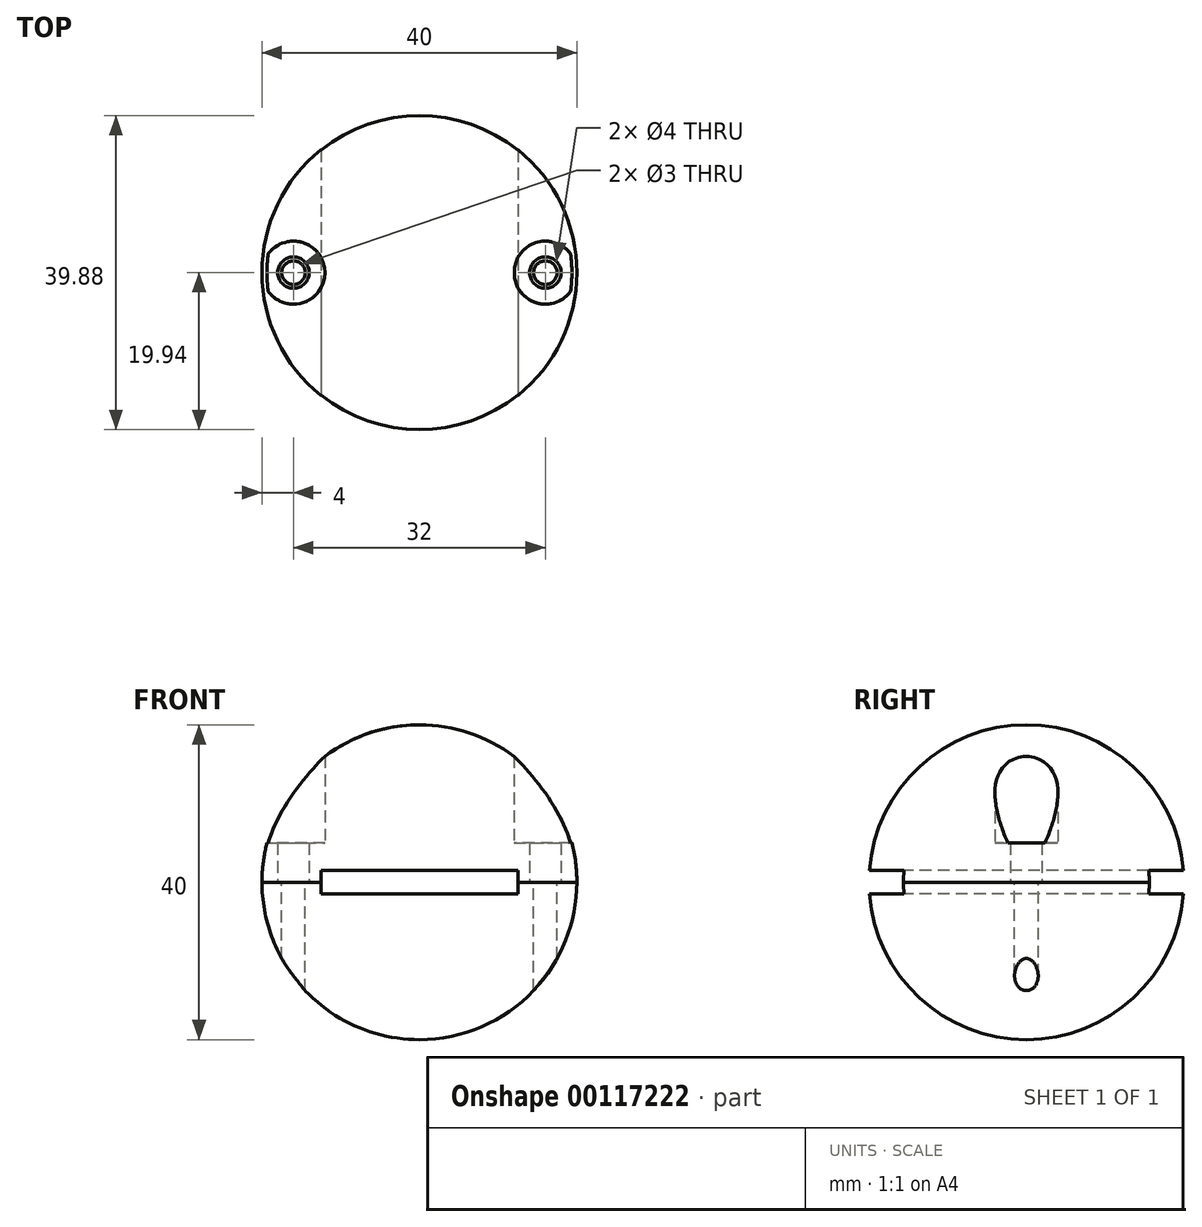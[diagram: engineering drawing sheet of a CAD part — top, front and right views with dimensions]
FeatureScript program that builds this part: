
annotation { "Feature Type Name" : "Feature", "Feature Type Description" : "" }
export const myFeature = defineFeature(function(context is Context, id is Id, definition is map)
    precondition{}
    {
        {
            var Q0;
            Q0=qCreatedBy(makeId("Front.planeOp"),FACE);
            var sketch = newSketch(context, id + "F0", { "sketchPlane" : qUnion([Q0])});
            skArc(sketch, "E0", {"start": v(0, 20) * mm, "mid": v(-14.14, 14.14) * mm, "end": v(-20, 0) * mm});
            skLineSegment(sketch, "E1", {"start": v(0, 0) * mm, "end": v(-20, 0) * mm});
            skLineSegment(sketch, "E2", {"start": v(0, 0) * mm, "end": v(0, 20) * mm});
            skPoint(sketch, "E3.left.end.orphan", {"position": v(12.5, 1.5) * mm});
            skPoint(sketch, "E3.bottom.start.orphan", {"position": v(12.5, -1.5) * mm});
            skPoint(sketch, "E4.orphan", {"position": v(-12.5, -1.5) * mm});
            skSolve(sketch);
        }
        {
            var Q0;
            Q0=makeQuery(id+"F0.imprint","IMPRINT",FACE,{"disambiguationData":[TD([[makeQuery(id+"F0.imprint","IMPRINT",EDGE,{"derivedFrom":sQuery(id+"F0.wireOp",EDGE,"E0")}),1.0]])]});
            var Q1;
            Q1=sQuery(id+"F0.wireOp",EDGE,"E2");
            revolve(context, id + "F1", {"entities" : qUnion([Q0]), "axis" : qUnion([Q1]), "revolveType" : RevolveType.FULL});
        }
        {
            var Q0;
            Q0=qCreatedBy(makeId("Front.planeOp"),FACE);
            var sketch = newSketch(context, id + "F2", { "sketchPlane" : qUnion([Q0])});
            skLineSegment(sketch, "E5.bottom", {"start": v(12.5, -1.5) * mm, "end": v(-12.5, -1.5) * mm});
            skLineSegment(sketch, "E5.top", {"start": v(12.5, 1.5) * mm, "end": v(-12.5, 1.5) * mm});
            skLineSegment(sketch, "E5.left", {"start": v(12.5, -1.5) * mm, "end": v(12.5, 1.5) * mm});
            skLineSegment(sketch, "E5.right", {"start": v(-12.5, -1.5) * mm, "end": v(-12.5, 1.5) * mm});
            skPoint(sketch, "E5.middle", {"position": v(0, 0) * mm});
            skSolve(sketch);
        }
        {
            var Q0;
            Q0=makeQuery(id+"F2.imprint","IMPRINT",FACE,{"disambiguationData":[TD([[makeQuery(id+"F2.imprint","IMPRINT",EDGE,{"derivedFrom":sQuery(id+"F2.wireOp",EDGE,"E5.bottom")}),-1.0]])]});
            extrude(context, id + "F3", {"entities" : qUnion([Q0]), "operationType" : NewBodyOperationType.REMOVE, "endBound" : BoundingType.SYMMETRIC, "oppositeDirection" : true, "depth" : 50 * mm});
        }
        {
            var Q0;
            Q0=makeQuery(id+"F3.boolean.opBoolean","SPLIT",FACE,{"disambiguationData":[TD([makeQuery(id+"F3.opExtrude","SWEPT_FACE",FACE,{"disambiguationData":[OSD([sQuery(id+"F2.wireOp",EDGE,"E5.right")])]})])],"derivedFrom":makeQuery(id+"F1.opRevolve","SWEPT_FACE",FACE,{"disambiguationData":[OSD([sQuery(id+"F0.wireOp",EDGE,"E1")])]})});
            var sketch = newSketch(context, id + "F4", { "sketchPlane" : qUnion([Q0])});
            skLineSegment(sketch, "E6", {"start": v(-20, 0) * mm, "end": v(20.22, 0) * mm, "construction": true});
            skCircle(sketch, "E7", {"center": v(-16, 0) * mm, "radius": 2 * mm});
            skCircle(sketch, "E8", {"center": v(16, 0) * mm, "radius": 2 * mm});
            skSolve(sketch);
        }
        {
            var Q0;
            Q0 = qSketchRegion(id + "F4", true);
            extrude(context, id + "F5", {"entities" : qUnion([Q0]), "operationType" : NewBodyOperationType.REMOVE, "endBound" : BoundingType.THROUGH_ALL, "oppositeDirection" : true, "depth" : 25 * mm});
        }
        {
            var Q0;
            Q0=makeQuery(id+"F3.boolean.opBoolean","SPLIT",FACE,{"disambiguationData":[TD([makeQuery(id+"F3.opExtrude","SWEPT_FACE",FACE,{"disambiguationData":[OSD([sQuery(id+"F2.wireOp",EDGE,"E5.left")])]})])],"derivedFrom":makeQuery(id+"F1.opRevolve","SWEPT_FACE",FACE,{"disambiguationData":[OSD([sQuery(id+"F0.wireOp",EDGE,"E1")])]})});
            cPlane(context, id + "F6", {"entities" : qUnion([Q0]), "cplaneType" : CPlaneType.OFFSET, "offset" : 5 * mm, "oppositeDirection" : true, "width" : 150 * mm, "height" : 150 * mm});
        }
        {
            var Q0;
            Q0=qCreatedBy(id+"F6.planeOp",FACE);
            var sketch = newSketch(context, id + "F7", { "sketchPlane" : qUnion([Q0])});
            skLineSegment(sketch, "E9", {"start": v(25.42, 0) * mm, "end": v(-24.4, 0) * mm, "construction": true});
            skLineSegment(sketch, "E10", {"start": v(0, -11.45) * mm, "end": v(0, 12.67) * mm, "construction": true});
            skCircle(sketch, "E11", {"center": v(-16, 0) * mm, "radius": 4 * mm});
            skCircle(sketch, "E12", {"center": v(16, 0) * mm, "radius": 4 * mm});
            skSolve(sketch);
        }
        {
            var Q0;
            Q0 = qSketchRegion(id + "F7", true);
            extrude(context, id + "F8", {"entities" : qUnion([Q0]), "operationType" : NewBodyOperationType.REMOVE, "endBound" : BoundingType.THROUGH_ALL, "oppositeDirection" : true, "depth" : 25 * mm});
        }
        {
            var Q0;
            Q0=qCreatedBy(makeId("Front.planeOp"),FACE);
            var sketch = newSketch(context, id + "F9", { "sketchPlane" : qUnion([Q0])});
            skArc(sketch, "E13", {"start": v(-20, 0) * mm, "mid": v(-14.14, -14.14) * mm, "end": v(0, -20) * mm});
            skLineSegment(sketch, "E14", {"start": v(0, 0) * mm, "end": v(0, -20) * mm});
            skLineSegment(sketch, "E15", {"start": v(0, 0) * mm, "end": v(-20, 0) * mm});
            skSolve(sketch);
        }
        {
            var Q0;
            Q0=makeQuery(id+"F9.imprint","IMPRINT",FACE,{"disambiguationData":[TD([[makeQuery(id+"F9.imprint","IMPRINT",EDGE,{"derivedFrom":sQuery(id+"F9.wireOp",EDGE,"E13")}),1.0]])]});
            var Q1;
            Q1=sQuery(id+"F9.wireOp",EDGE,"E14");
            revolve(context, id + "F10", {"entities" : qUnion([Q0]), "axis" : qUnion([Q1]), "revolveType" : RevolveType.FULL});
        }
        {
            var Q0;
            Q0=qCreatedBy(makeId("Front.planeOp"),FACE);
            var sketch = newSketch(context, id + "F11", { "sketchPlane" : qUnion([Q0])});
            skLineSegment(sketch, "E16.bottom", {"start": v(-12.5, 1.5) * mm, "end": v(12.5, 1.5) * mm});
            skLineSegment(sketch, "E16.top", {"start": v(-12.5, -1.5) * mm, "end": v(12.5, -1.5) * mm});
            skLineSegment(sketch, "E16.left", {"start": v(-12.5, 1.5) * mm, "end": v(-12.5, -1.5) * mm});
            skLineSegment(sketch, "E16.right", {"start": v(12.5, 1.5) * mm, "end": v(12.5, -1.5) * mm});
            skPoint(sketch, "E16.middle", {"position": v(0, 0) * mm});
            skSolve(sketch);
        }
        {
            var Q0;
            Q0=makeQuery(id+"F11.imprint","IMPRINT",FACE,{"disambiguationData":[TD([[makeQuery(id+"F11.imprint","IMPRINT",EDGE,{"derivedFrom":sQuery(id+"F11.wireOp",EDGE,"E16.bottom")}),-1.0]])]});
            extrude(context, id + "F12", {"entities" : qUnion([Q0]), "operationType" : NewBodyOperationType.REMOVE, "endBound" : BoundingType.SYMMETRIC, "oppositeDirection" : true, "depth" : 50 * mm});
        }
        {
            var Q0;
            Q0=qCreatedBy(makeId("Top.planeOp"),FACE);
            var sketch = newSketch(context, id + "F13", { "sketchPlane" : qUnion([Q0])});
            skLineSegment(sketch, "E17", {"start": v(0, 46.68) * mm, "end": v(0, -45.24) * mm, "construction": true});
            skLineSegment(sketch, "E18", {"start": v(-36.87, 0) * mm, "end": v(39.05, 0) * mm, "construction": true});
            skCircle(sketch, "E19", {"center": v(-16, 0) * mm, "radius": 1.5 * mm});
            skCircle(sketch, "E20", {"center": v(16, 0) * mm, "radius": 1.5 * mm});
            skSolve(sketch);
        }
        {
            var Q0;
            Q0 = qSketchRegion(id + "F13", true);
            extrude(context, id + "F14", {"entities" : qUnion([Q0]), "operationType" : NewBodyOperationType.REMOVE, "endBound" : BoundingType.THROUGH_ALL, "oppositeDirection" : true, "depth" : 25 * mm});
        }
    });
